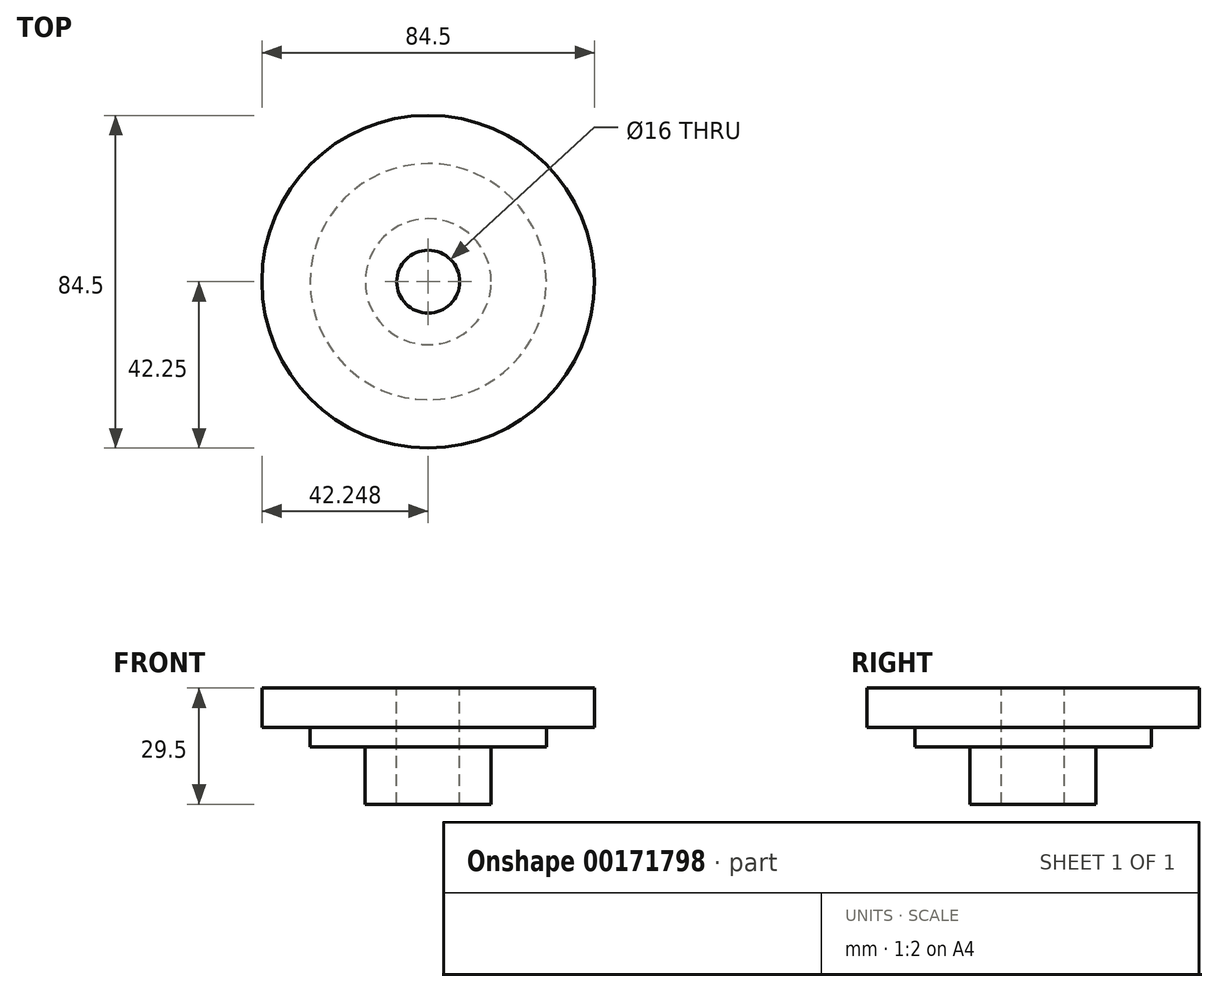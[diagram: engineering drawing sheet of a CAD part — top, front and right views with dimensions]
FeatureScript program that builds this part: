
annotation { "Feature Type Name" : "Feature", "Feature Type Description" : "" }
export const myFeature = defineFeature(function(context is Context, id is Id, definition is map)
    precondition{}
    {
        {
            var Q0;
            Q0=qCreatedBy(makeId("Front.planeOp"),FACE);
            var sketch = newSketch(context, id + "F0", { "sketchPlane" : qUnion([Q0])});
            skLineSegment(sketch, "E0", {"start": v(-0.01, 75.37) * mm, "end": v(-0.01, -82.81) * mm, "construction": true});
            skLineSegment(sketch, "E1", {"start": v(42.24, 19.45) * mm, "end": v(29.99, 19.45) * mm});
            skLineSegment(sketch, "E2", {"start": v(15.99, 4.95) * mm, "end": v(15.99, -0.05) * mm});
            skLineSegment(sketch, "E3", {"start": v(29.99, 19.45) * mm, "end": v(29.99, 14.45) * mm});
            skLineSegment(sketch, "E4", {"start": v(42.24, 19.45) * mm, "end": v(42.24, 29.45) * mm});
            skLineSegment(sketch, "E5", {"start": v(42.24, 29.45) * mm, "end": v(7.99, 29.45) * mm});
            skLineSegment(sketch, "E6", {"start": v(7.99, 29.45) * mm, "end": v(7.99, -0.05) * mm});
            skLineSegment(sketch, "E7", {"start": v(7.99, -0.05) * mm, "end": v(15.99, -0.05) * mm});
            skLineSegment(sketch, "E8", {"start": v(29.99, 14.45) * mm, "end": v(24.99, 14.45) * mm});
            skLineSegment(sketch, "E9", {"start": v(15.99, 4.95) * mm, "end": v(15.99, 14.45) * mm});
            skLineSegment(sketch, "E10", {"start": v(15.99, 14.45) * mm, "end": v(24.99, 14.45) * mm});
            skSolve(sketch);
        }
        {
            var Q0;
            Q0 = qSketchRegion(id + "F0", true);
            var Q1;
            Q1=sQuery(id+"F0.wireOp",EDGE,"E0");
            revolve(context, id + "F1", {"entities" : qUnion([Q0]), "axis" : qUnion([Q1]), "revolveType" : RevolveType.FULL});
        }
    });
